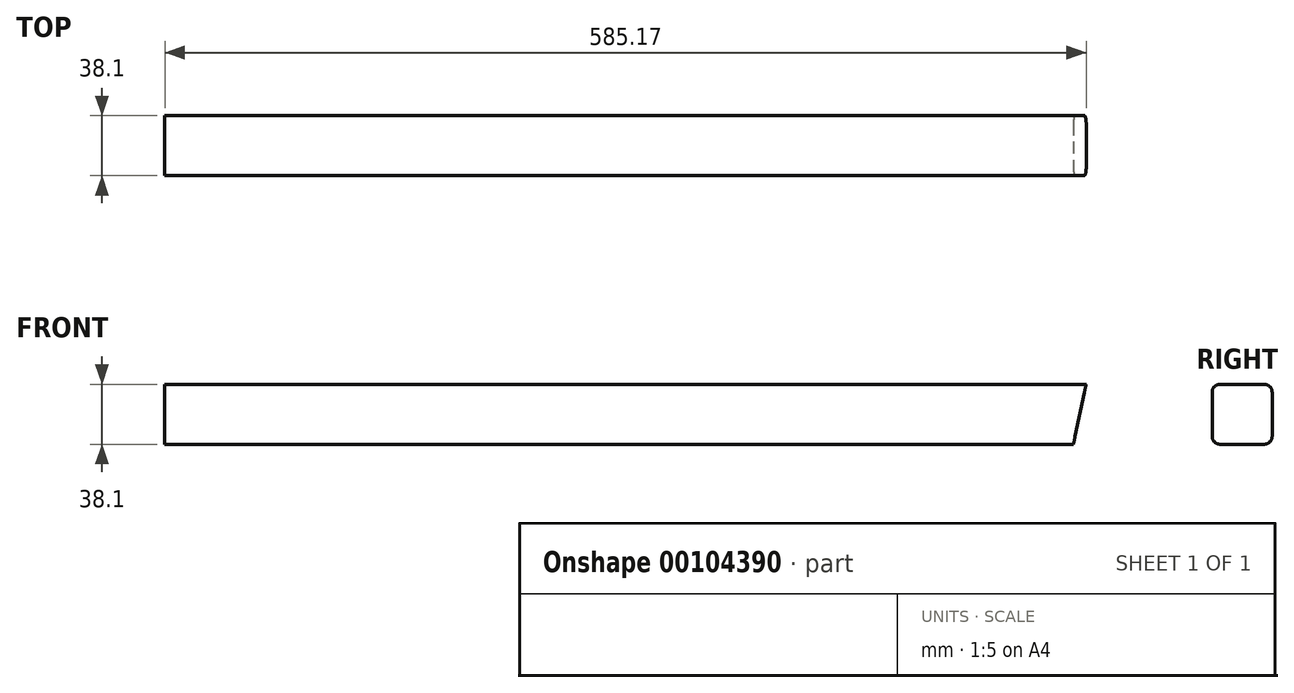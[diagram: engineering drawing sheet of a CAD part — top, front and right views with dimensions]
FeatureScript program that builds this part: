
annotation { "Feature Type Name" : "Feature", "Feature Type Description" : "" }
export const myFeature = defineFeature(function(context is Context, id is Id, definition is map)
    precondition{}
    {
        {
            var Q0;
            Q0=qCreatedBy(makeId("Front.planeOp"),FACE);
            var sketch = newSketch(context, id + "F0", { "sketchPlane" : qUnion([Q0])});
            skLineSegment(sketch, "E0.bottom", {"start": v(313.94, -19.05) * mm, "end": v(-313.94, -19.05) * mm});
            skLineSegment(sketch, "E0.top", {"start": v(313.94, 19.05) * mm, "end": v(-313.94, 19.05) * mm});
            skLineSegment(sketch, "E0.left", {"start": v(313.94, -19.05) * mm, "end": v(313.94, 19.05) * mm});
            skLineSegment(sketch, "E0.right", {"start": v(-313.94, -19.05) * mm, "end": v(-313.94, 19.05) * mm});
            skPoint(sketch, "E0.middle", {"position": v(0, 0) * mm});
            skSolve(sketch);
        }
        {
            var Q0;
            Q0 = qSketchRegion(id + "F0", true);
            extrude(context, id + "F1", {"entities" : qUnion([Q0]), "endBound" : BoundingType.SYMMETRIC, "depth" : 38.1 * mm});
        }
        {
            var Q0;
            Q0=makeQuery(id+"F1.opExtrude","CAP_FACE",FACE,{"disambiguationData":[OSD([sQuery(id+"F0.wireOp",EDGE,"E0.bottom"),sQuery(id+"F0.wireOp",EDGE,"E0.top"),sQuery(id+"F0.wireOp",EDGE,"E0.left"),sQuery(id+"F0.wireOp",EDGE,"E0.right")])],"isStart":false});
            var sketch = newSketch(context, id + "F2", { "sketchPlane" : qUnion([Q0])});
            skLineSegment(sketch, "E1", {"start": v(271.23, 19.05) * mm, "end": v(263.13, -19.05) * mm});
            skLineSegment(sketch, "E2", {"start": v(263.13, -19.05) * mm, "end": v(313.94, -19.05) * mm});
            skLineSegment(sketch, "E3", {"start": v(313.94, -19.05) * mm, "end": v(313.94, 19.05) * mm});
            skLineSegment(sketch, "E4", {"start": v(313.94, 19.05) * mm, "end": v(271.23, 19.05) * mm});
            skLineSegment(sketch, "E5", {"start": v(267.18, 0) * mm, "end": v(313.94, 0) * mm, "construction": true});
            skSolve(sketch);
        }
        {
            var Q0;
            Q0 = qSketchRegion(id + "F2", true);
            extrude(context, id + "F3", {"entities" : qUnion([Q0]), "operationType" : NewBodyOperationType.REMOVE, "endBound" : BoundingType.THROUGH_ALL, "oppositeDirection" : true, "depth" : 25.4 * mm});
        }
        {
            var Q0;
            Q0=makeQuery(id+"F1.opExtrude","CAP_EDGE",EDGE,{"disambiguationData":[OSD([sQuery(id+"F0.wireOp",EDGE,"E0.top")])],"isStart":false});
            var Q1;
            Q1=makeQuery(id+"F1.opExtrude","CAP_EDGE",EDGE,{"disambiguationData":[OSD([sQuery(id+"F0.wireOp",EDGE,"E0.bottom")])],"isStart":false});
            var Q2;
            Q2=makeQuery(id+"F1.opExtrude","CAP_EDGE",EDGE,{"disambiguationData":[OSD([sQuery(id+"F0.wireOp",EDGE,"E0.top")])],"isStart":true});
            var Q3;
            Q3=makeQuery(id+"F1.opExtrude","CAP_EDGE",EDGE,{"disambiguationData":[OSD([sQuery(id+"F0.wireOp",EDGE,"E0.bottom")])],"isStart":true});
            fillet(context, id + "F4", {"entities" : qUnion([Q0, Q1, Q2, Q3]), "radius" : 5.08 * mm, "tangentPropagation" : true, "allowEdgeOverflow" : false});
        }
    });
